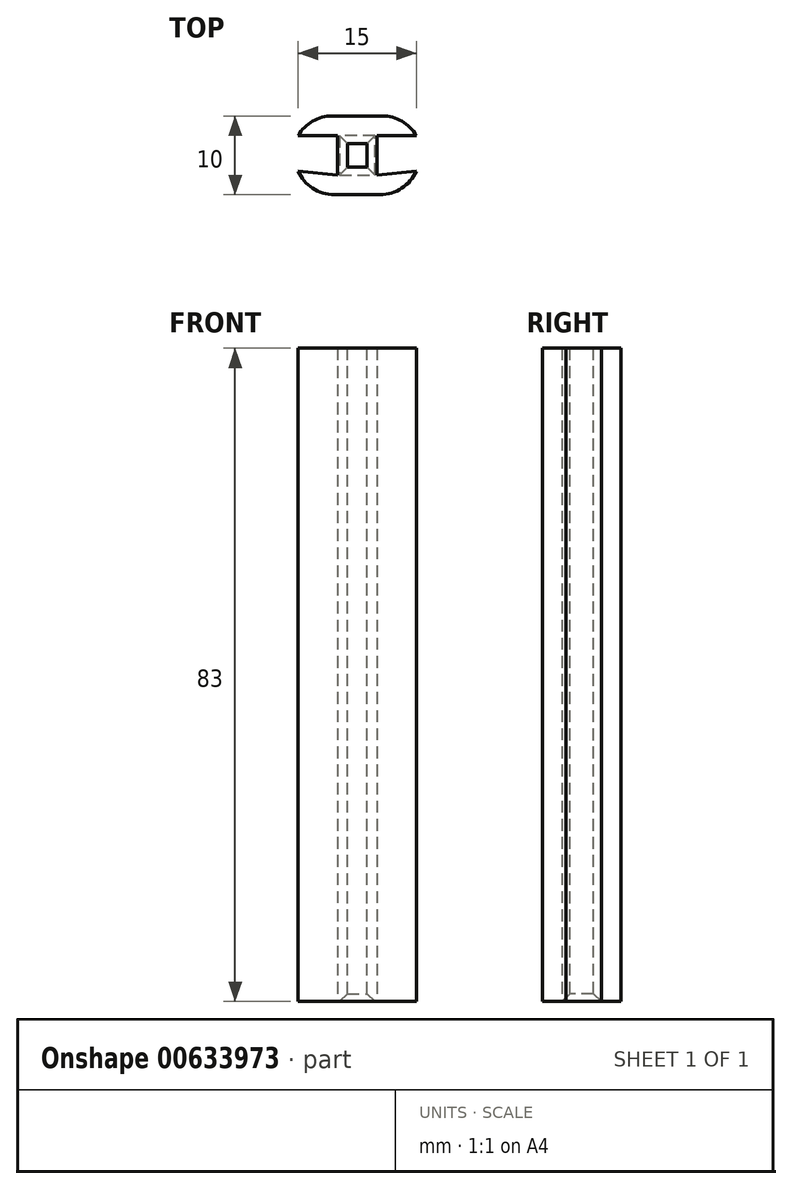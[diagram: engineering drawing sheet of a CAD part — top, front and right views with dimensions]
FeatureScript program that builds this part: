
annotation { "Feature Type Name" : "Feature", "Feature Type Description" : "" }
export const myFeature = defineFeature(function(context is Context, id is Id, definition is map)
    precondition{}
    {
        {
            var Q0;
            Q0=qCreatedBy(makeId("Top.planeOp"),FACE);
            var sketch = newSketch(context, id + "F0", { "sketchPlane" : qUnion([Q0])});
            skLineSegment(sketch, "E0", {"start": v(0, 5) * mm, "end": v(-7.5, 5) * mm});
            skLineSegment(sketch, "E1", {"start": v(-7.5, 5) * mm, "end": v(-7.5, 2.5) * mm});
            skLineSegment(sketch, "E2", {"start": v(-7.5, 2.5) * mm, "end": v(-2.5, 2.5) * mm});
            skLineSegment(sketch, "E3", {"start": v(-2.5, 2.5) * mm, "end": v(-2.5, -2.5) * mm});
            skLineSegment(sketch, "E4", {"start": v(-2.5, -2.5) * mm, "end": v(-7.5, -2.5) * mm});
            skLineSegment(sketch, "E5", {"start": v(-7.5, -2.5) * mm, "end": v(-7.5, -5) * mm});
            skLineSegment(sketch, "E6", {"start": v(-7.5, -5) * mm, "end": v(0, -5) * mm});
            skLineSegment(sketch, "E7", {"start": v(0, -5) * mm, "end": v(0, 5) * mm});
            skLineSegment(sketch, "E8", {"start": v(-7.5, -2.5) * mm, "end": v(-7.5, -2) * mm});
            skLineSegment(sketch, "E9", {"start": v(-7.5, -2) * mm, "end": v(-2.5, -2.5) * mm});
            skSolve(sketch);
        }
        {
            var Q0;
            Q0=makeQuery(id+"F0.imprint","IMPRINT",FACE,{"disambiguationData":[TD([[makeQuery(id+"F0.imprint","IMPRINT",EDGE,{"derivedFrom":sQuery(id+"F0.wireOp",EDGE,"E0")}),1.0]])]});
            var Q1;
            Q1=makeQuery(id+"F0.imprint","IMPRINT",FACE,{"disambiguationData":[TD([[makeQuery(id+"F0.imprint","IMPRINT",EDGE,{"derivedFrom":sQuery(id+"F0.wireOp",EDGE,"E4")}),-1.0]])]});
            extrude(context, id + "F1", {"entities" : qUnion([Q0, Q1]), "depth" : 83 * mm, "offsetDistance" : 25 * mm});
        }
        {
            var Q0;
            Q0=makeQuery(id+"F1.opExtrude","SWEPT_EDGE",EDGE,{"disambiguationData":[OSD([sQuery(id+"F0.wireOp",EDGE,"E0"),sQuery(id+"F0.wireOp",EDGE,"E1")])]});
            var Q1;
            Q1=makeQuery(id+"F1.opExtrude","SWEPT_EDGE",EDGE,{"disambiguationData":[OSD([sQuery(id+"F0.wireOp",EDGE,"E5"),sQuery(id+"F0.wireOp",EDGE,"E6")])]});
            fillet(context, id + "F2", {"entities" : qUnion([Q0, Q1]), "radius" : 5 * mm, "tangentPropagation" : true, "allowEdgeOverflow" : false});
        }
        {
            var Q0;
            Q0=makeQuery(id+"F1.opExtrude","SWEPT_BODY",BODY,{"disambiguationData":[OSD([sQuery(id+"F0.wireOp",EDGE,"E0"),sQuery(id+"F0.wireOp",EDGE,"E1"),sQuery(id+"F0.wireOp",EDGE,"E2"),sQuery(id+"F0.wireOp",EDGE,"E3"),sQuery(id+"F0.wireOp",EDGE,"E5"),sQuery(id+"F0.wireOp",EDGE,"E6"),sQuery(id+"F0.wireOp",EDGE,"E7"),sQuery(id+"F0.wireOp",EDGE,"E8"),sQuery(id+"F0.wireOp",EDGE,"E9")])]});
            var Q1;
            Q1=makeQuery(id+"F1.opExtrude","SWEPT_FACE",FACE,{"disambiguationData":[OSD([sQuery(id+"F0.wireOp",EDGE,"E7")])]});
            mirror(context, id + "F3", {"operationType" : NewBodyOperationType.ADD, "entities" : qUnion([Q0]), "mirrorPlane" : qUnion([Q1])});
        }
        {
            var Q0;
            {var subQ0=makeQuery(id+"F1.opExtrude","CAP_FACE",FACE,{"disambiguationData":[OSD([sQuery(id+"F0.wireOp",EDGE,"E0"),sQuery(id+"F0.wireOp",EDGE,"E1"),sQuery(id+"F0.wireOp",EDGE,"E2"),sQuery(id+"F0.wireOp",EDGE,"E3"),sQuery(id+"F0.wireOp",EDGE,"E5"),sQuery(id+"F0.wireOp",EDGE,"E6"),sQuery(id+"F0.wireOp",EDGE,"E7"),sQuery(id+"F0.wireOp",EDGE,"E8"),sQuery(id+"F0.wireOp",EDGE,"E9")])],"isStart":false});Q0=makeQuery(id+"F3.boolean.opBoolean","MERGE",FACE,{"derivedFrom":[subQ0,makeQuery(id+"F3.opPattern","COPY",FACE,{"derivedFrom":subQ0,"instanceName":"1"})]});}
            var sketch = newSketch(context, id + "F4", { "sketchPlane" : qUnion([Q0])});
            skLineSegment(sketch, "E10.bottom", {"start": v(1.25, 1.5) * mm, "end": v(-1.25, 1.5) * mm});
            skLineSegment(sketch, "E10.top", {"start": v(1.25, -1.5) * mm, "end": v(-1.25, -1.5) * mm});
            skLineSegment(sketch, "E10.left", {"start": v(1.25, 1.5) * mm, "end": v(1.25, -1.5) * mm});
            skLineSegment(sketch, "E10.right", {"start": v(-1.25, 1.5) * mm, "end": v(-1.25, -1.5) * mm});
            skPoint(sketch, "E10.middle", {"position": v(0, 0) * mm});
            skSolve(sketch);
        }
        {
            var Q0;
            Q0=makeQuery(id+"F4.imprint","IMPRINT",FACE,{"disambiguationData":[TD([[makeQuery(id+"F4.imprint","IMPRINT",EDGE,{"derivedFrom":sQuery(id+"F4.wireOp",EDGE,"E10.bottom")}),1.0]])]});
            extrude(context, id + "F5", {"entities" : qUnion([Q0]), "operationType" : NewBodyOperationType.REMOVE, "endBound" : BoundingType.THROUGH_ALL, "oppositeDirection" : true, "depth" : 25 * mm, "offsetDistance" : 25 * mm});
        }
        {
            var Q0;
            Q0=makeQuery(id+"F5.boolean.opBoolean","COPY",EDGE,{"derivedFrom":makeQuery(id+"F5.opExtrude","CAP_EDGE",EDGE,{"disambiguationData":[OSD([sQuery(id+"F4.wireOp",EDGE,"E10.left")])],"isStart":true})});
            var Q1;
            Q1=makeQuery(id+"F5.boolean.opBoolean","COPY",EDGE,{"derivedFrom":makeQuery(id+"F5.opExtrude","CAP_EDGE",EDGE,{"disambiguationData":[OSD([sQuery(id+"F4.wireOp",EDGE,"E10.bottom")])],"isStart":true})});
            var Q2;
            Q2=makeQuery(id+"F5.boolean.opBoolean","COPY",EDGE,{"derivedFrom":makeQuery(id+"F5.opExtrude","CAP_EDGE",EDGE,{"disambiguationData":[OSD([sQuery(id+"F4.wireOp",EDGE,"E10.right")])],"isStart":true})});
            var Q3;
            Q3=makeQuery(id+"F5.boolean.opBoolean","COPY",EDGE,{"derivedFrom":makeQuery(id+"F5.opExtrude","CAP_EDGE",EDGE,{"disambiguationData":[OSD([sQuery(id+"F4.wireOp",EDGE,"E10.top")])],"isStart":true})});
            var Q4;
            {var subQ0=makeQuery(id+"F1.opExtrude","CAP_FACE",FACE,{"disambiguationData":[OSD([sQuery(id+"F0.wireOp",EDGE,"E0"),sQuery(id+"F0.wireOp",EDGE,"E1"),sQuery(id+"F0.wireOp",EDGE,"E2"),sQuery(id+"F0.wireOp",EDGE,"E3"),sQuery(id+"F0.wireOp",EDGE,"E5"),sQuery(id+"F0.wireOp",EDGE,"E6"),sQuery(id+"F0.wireOp",EDGE,"E7"),sQuery(id+"F0.wireOp",EDGE,"E8"),sQuery(id+"F0.wireOp",EDGE,"E9")])],"isStart":true});Q4=makeQuery(id+"F5.boolean.opBoolean","INTERSECT",EDGE,{"derivedFrom":[makeQuery(id+"F3.boolean.opBoolean","MERGE",FACE,{"derivedFrom":[subQ0,makeQuery(id+"F3.opPattern","COPY",FACE,{"derivedFrom":subQ0,"instanceName":"1"})]}),makeQuery(id+"F5.opExtrude","SWEPT_FACE",FACE,{"disambiguationData":[OSD([sQuery(id+"F4.wireOp",EDGE,"E10.left")])]})]});}
            var Q5;
            {var subQ0=makeQuery(id+"F1.opExtrude","CAP_FACE",FACE,{"disambiguationData":[OSD([sQuery(id+"F0.wireOp",EDGE,"E0"),sQuery(id+"F0.wireOp",EDGE,"E1"),sQuery(id+"F0.wireOp",EDGE,"E2"),sQuery(id+"F0.wireOp",EDGE,"E3"),sQuery(id+"F0.wireOp",EDGE,"E5"),sQuery(id+"F0.wireOp",EDGE,"E6"),sQuery(id+"F0.wireOp",EDGE,"E7"),sQuery(id+"F0.wireOp",EDGE,"E8"),sQuery(id+"F0.wireOp",EDGE,"E9")])],"isStart":true});Q5=makeQuery(id+"F5.boolean.opBoolean","INTERSECT",EDGE,{"derivedFrom":[makeQuery(id+"F3.boolean.opBoolean","MERGE",FACE,{"derivedFrom":[subQ0,makeQuery(id+"F3.opPattern","COPY",FACE,{"derivedFrom":subQ0,"instanceName":"1"})]}),makeQuery(id+"F5.opExtrude","SWEPT_FACE",FACE,{"disambiguationData":[OSD([sQuery(id+"F4.wireOp",EDGE,"E10.top")])]})]});}
            var Q6;
            {var subQ0=makeQuery(id+"F1.opExtrude","CAP_FACE",FACE,{"disambiguationData":[OSD([sQuery(id+"F0.wireOp",EDGE,"E0"),sQuery(id+"F0.wireOp",EDGE,"E1"),sQuery(id+"F0.wireOp",EDGE,"E2"),sQuery(id+"F0.wireOp",EDGE,"E3"),sQuery(id+"F0.wireOp",EDGE,"E5"),sQuery(id+"F0.wireOp",EDGE,"E6"),sQuery(id+"F0.wireOp",EDGE,"E7"),sQuery(id+"F0.wireOp",EDGE,"E8"),sQuery(id+"F0.wireOp",EDGE,"E9")])],"isStart":true});Q6=makeQuery(id+"F5.boolean.opBoolean","INTERSECT",EDGE,{"derivedFrom":[makeQuery(id+"F3.boolean.opBoolean","MERGE",FACE,{"derivedFrom":[subQ0,makeQuery(id+"F3.opPattern","COPY",FACE,{"derivedFrom":subQ0,"instanceName":"1"})]}),makeQuery(id+"F5.opExtrude","SWEPT_FACE",FACE,{"disambiguationData":[OSD([sQuery(id+"F4.wireOp",EDGE,"E10.right")])]})]});}
            var Q7;
            {var subQ0=makeQuery(id+"F1.opExtrude","CAP_FACE",FACE,{"disambiguationData":[OSD([sQuery(id+"F0.wireOp",EDGE,"E0"),sQuery(id+"F0.wireOp",EDGE,"E1"),sQuery(id+"F0.wireOp",EDGE,"E2"),sQuery(id+"F0.wireOp",EDGE,"E3"),sQuery(id+"F0.wireOp",EDGE,"E5"),sQuery(id+"F0.wireOp",EDGE,"E6"),sQuery(id+"F0.wireOp",EDGE,"E7"),sQuery(id+"F0.wireOp",EDGE,"E8"),sQuery(id+"F0.wireOp",EDGE,"E9")])],"isStart":true});Q7=makeQuery(id+"F5.boolean.opBoolean","INTERSECT",EDGE,{"derivedFrom":[makeQuery(id+"F3.boolean.opBoolean","MERGE",FACE,{"derivedFrom":[subQ0,makeQuery(id+"F3.opPattern","COPY",FACE,{"derivedFrom":subQ0,"instanceName":"1"})]}),makeQuery(id+"F5.opExtrude","SWEPT_FACE",FACE,{"disambiguationData":[OSD([sQuery(id+"F4.wireOp",EDGE,"E10.bottom")])]})]});}
            chamfer(context, id + "F6", {"entities" : qUnion([Q0, Q1, Q2, Q3, Q4, Q5, Q6, Q7]), "width" : 1 * mm, "tangentPropagation" : true});
        }
    });
